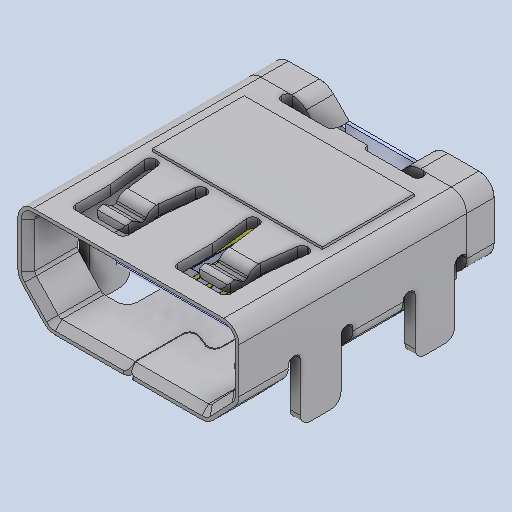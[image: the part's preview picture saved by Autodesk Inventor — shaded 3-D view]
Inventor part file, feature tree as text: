
AUTODESK INVENTOR PART (.ipt)
format: ipt  version: 2024.3 (Build 283343000, 343)  size: 996,352 bytes
history: native  units: in
note: dims shown in document units (in); Inventor stores cm internally (conversion verified against a paired STEP export)
features: other x40, chamfer x3, fillet x1
ambient origin geometry x8: Origin, YZ Plane, XZ Plane, XY Plane, X Axis, Y Axis, Z Axis, Center Point
bodies: Solid1 (feature_tree), Solid2 (feature_tree), Solid3 (feature_tree), Solid4 (feature_tree), Solid5 (feature_tree), Solid6 (feature_tree), Solid7 (feature_tree), Solid8 (feature_tree), Solid9 (feature_tree), Solid10 (feature_tree), Solid11 (feature_tree), Solid12 (feature_tree), Solid13 (feature_tree), Solid14 (feature_tree), Solid15 (feature_tree), Solid16 (feature_tree), Solid17 (feature_tree), Solid18 (feature_tree), Solid19 (feature_tree), Solid20 (feature_tree), Solid21 (feature_tree), Solid22 (feature_tree), Solid23 (feature_tree), Solid24 (feature_tree), Solid25 (feature_tree), Solid26 (feature_tree), Solid27 (feature_tree), Solid28 (feature_tree), Solid29 (feature_tree), Solid30 (feature_tree), Solid31 (feature_tree), Solid32 (feature_tree), Solid33 (feature_tree), Solid34 (feature_tree), Solid35 (feature_tree), Solid36 (feature_tree), Solid37 (feature_tree), Solid38 (feature_tree), Solid39 (feature_tree), Solid40 (feature_tree), Solid41 (feature_tree), Solid42 (feature_tree), Solid43 (feature_tree), Solid44 (feature_tree), Solid45 (feature_tree)
feature tree (44):
  other  "Cut-Extrude2"
  fillet  "Fillet2"  [1 undecoded]
  other  "LPattern1[1]"
  other  "LPattern1[2]"
  other  "LPattern1[3]"
  other  "LPattern1[4]"
  other  "LPattern1[5]"
  other  "LPattern1[6]"
  other  "LPattern1[7]"
  other  "LPattern1[8]"
  other  "LPattern1[9]"
  other  "Boss-Extrude4"
  other  "LPattern2[1]"
  other  "LPattern2[2]"
  other  "LPattern2[3]"
  other  "LPattern2[4]"
  other  "LPattern2[5]"
  other  "LPattern2[6]"
  other  "LPattern2[7]"
  other  "LPattern2[8]"
  other  "LPattern3[1]"
  other  "LPattern3[2]"
  other  "LPattern3[3]"
  other  "LPattern3[4]"
  other  "LPattern3[5]"
  other  "LPattern3[6]"
  other  "LPattern3[7]"
  other  "LPattern3[8]"
  other  "Boss-Extrude9"
  other  "LPattern4[1]"
  other  "LPattern4[2]"
  other  "LPattern4[3]"
  other  "LPattern4[4]"
  other  "LPattern4[5]"
  other  "LPattern4[6]"
  other  "LPattern4[7]"
  other  "LPattern4[8]"
  other  "Cut-Extrude13[1]"
  other  "Cut-Extrude13[2]"
  other  "Boss-Extrude15[2]"
  chamfer  "Chamfer6"  [1 undecoded]
  chamfer  "Chamfer5"  [1 undecoded]
  other  "Cut-Extrude18[3]"
  chamfer  "Chamfer7"  [1 undecoded]
note: 4 required parameter values undecoded (feature->parameter linkage not recoverable at this tier; creation-order binding heuristic only, values carry confidence <= 0.55)
